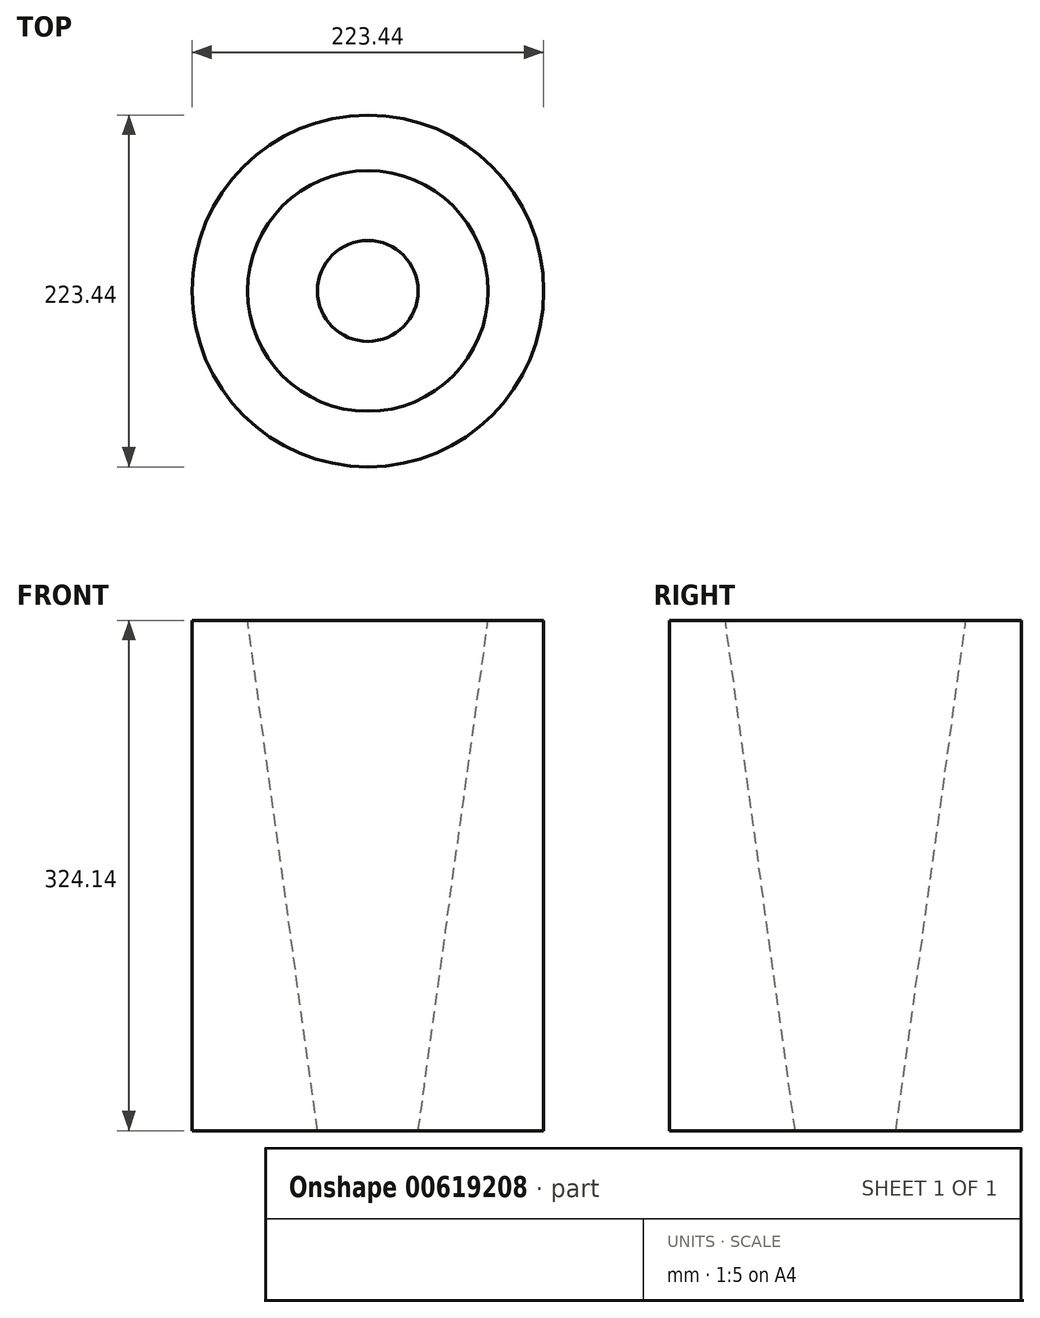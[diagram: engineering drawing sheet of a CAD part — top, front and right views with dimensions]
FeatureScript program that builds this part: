
annotation { "Feature Type Name" : "Feature", "Feature Type Description" : "" }
export const myFeature = defineFeature(function(context is Context, id is Id, definition is map)
    precondition{}
    {
        {
            var Q0;
            Q0=qCreatedBy(makeId("Top.planeOp"),FACE);
            var sketch = newSketch(context, id + "F0", { "sketchPlane" : qUnion([Q0])});
            skCircle(sketch, "E0", {"center": v(0, 0) * mm, "radius": 111.72 * mm});
            skSolve(sketch);
        }
        {
            var Q0;
            Q0=makeQuery(id+"F0.imprint","IMPRINT",FACE,{"disambiguationData":[TD([[makeQuery(id+"F0.imprint","IMPRINT",EDGE,{"derivedFrom":sQuery(id+"F0.wireOp",EDGE,"E0")}),1.0]])]});
            extrude(context, id + "F1", {"entities" : qUnion([Q0]), "depth" : 324.14 * mm, "offsetDistance" : 25.4 * mm});
        }
        {
            var Q0;
            Q0=makeQuery(id+"F1.opExtrude","CAP_FACE",FACE,{"disambiguationData":[OSD([sQuery(id+"F0.wireOp",EDGE,"E0")])],"isStart":false});
            var sketch = newSketch(context, id + "F2", { "sketchPlane" : qUnion([Q0])});
            skCircle(sketch, "E1", {"center": v(0, 0) * mm, "radius": 76.44 * mm});
            skSolve(sketch);
        }
        {
            var Q0;
            Q0=makeQuery(id+"F1.opExtrude","CAP_FACE",FACE,{"disambiguationData":[OSD([sQuery(id+"F0.wireOp",EDGE,"E0")])],"isStart":true});
            var sketch = newSketch(context, id + "F3", { "sketchPlane" : qUnion([Q0])});
            skCircle(sketch, "E2", {"center": v(0, 0) * mm, "radius": 32 * mm});
            skSolve(sketch);
        }
        {
            var Q1;
            Q1 = qSketchRegion(id + "F3", true);
            var Q2;
            Q2 = qSketchRegion(id + "F2", true);
            loft(context, id + "F4", {"operationType" : NewBodyOperationType.REMOVE, "sheetProfilesArray" : [{ "sheetProfileEntities" : qUnion([Q1]) }, { "sheetProfileEntities" : qUnion([Q2]) }]});
        }
    });
